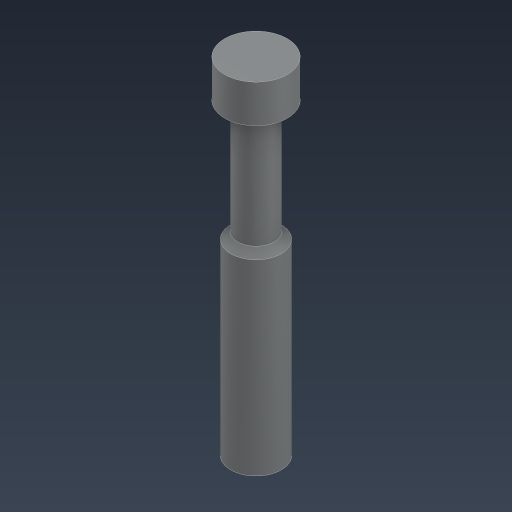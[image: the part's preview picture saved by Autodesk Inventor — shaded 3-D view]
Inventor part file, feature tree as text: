
AUTODESK INVENTOR PART (.ipt)
format: ipt  version: 2024.3 (Build 283343000, 343)  size: 107,520 bytes
history: native  units: in
note: dims shown in document units (in); Inventor stores cm internally (conversion verified against a paired STEP export)
features: other x1, chamfer x1
ambient origin geometry x8: Origin, YZ Plane, XZ Plane, XY Plane, X Axis, Y Axis, Z Axis, Center Point
bodies: Solid1 (feature_tree)
feature tree (2):
  other  "Pneumatic Fitting Plug1"
  chamfer  "Chamfer1"  [1 undecoded]
note: 1 required parameter value undecoded (feature->parameter linkage not recoverable at this tier; creation-order binding heuristic only, values carry confidence <= 0.55)
